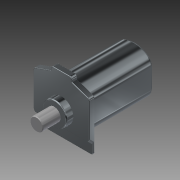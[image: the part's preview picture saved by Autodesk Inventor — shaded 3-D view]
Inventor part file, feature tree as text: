
AUTODESK INVENTOR PART (.ipt)
format: ipt  version: 2018 (Build 220112000, 112)  size: 286,208 bytes
history: native  units: mm
features: fillet x8, extrude x7, sketch x6, chamfer x2
ambient origin geometry x8: Origin, YZ Plane, XZ Plane, XY Plane, X Axis, Y Axis, Z Axis, Center Point
bodies: Solid1 (feature_tree)
feature tree (23):
  extrude  "Extrusion1"  Depth=55.3mm TaperAngle=0.0deg
  sketch  "Sketch2"  dims[d4=53.2mm d5=11.0mm d6=55.3mm d7=0.0mm d8=2.0mm]
  extrude  "Extrusion2"  Depth=2.0mm
  fillet  "Fillet2"  Radius=55.3mm
  fillet  "Fillet1"  Radius=2.0mm
  extrude  "Extrusion3"  Depth=12.9mm
  fillet  "Fillet3"  Radius=6.4mm
  extrude  "Extrusion4"  Depth=2.0mm
  extrude  "Extrusion5"  Depth=1.5mm TaperAngle=0.0deg
  chamfer  "Chamfer1"  Distance=4.5mm
  fillet  "Fillet4"  Radius=2.0mm
  fillet  "Fillet5"  Radius=2.0mm
  fillet  "Fillet6"  Radius=0.5mm
  fillet  "Fillet7"  Radius=45.0mm
  extrude  "Extrusion6"  Depth=2.0mm
  extrude  "Extrusion7"  Depth=2.0mm
  fillet  "Fillet8"  Radius=19.3mm
  chamfer  "Chamfer2"  Distance=5.7mm
  sketch  "Sketch1"  dims[d0=36.0mm d1=55.3mm d2=0.0mm]
  sketch  "Sketch3"  dims[d9=8.0mm d10=12.9mm d11=6.4mm d12=0.0mm]
  sketch  "Sketch4"  dims[d13=0.9mm d15=2.0mm]
  sketch  "Sketch5"  dims[d16=2.0mm d17=1.5mm d18=0.0mm d19=4.5mm d20=0.0mm]
  sketch  "Sketch6"  dims[d21=3.0mm d22=2.0mm d23=45.0deg d24=2.0mm d25=2.0mm d26=0.5mm d28=45.0mm d29=17.0mm d30=2.0mm d31=19.3mm d32=5.7mm d33=0.0mm d34=10.5mm d35=14.3mm d36=0.0mm d37=1.0mm d38=0.5mm d39=2.0mm d40=45.0deg]
